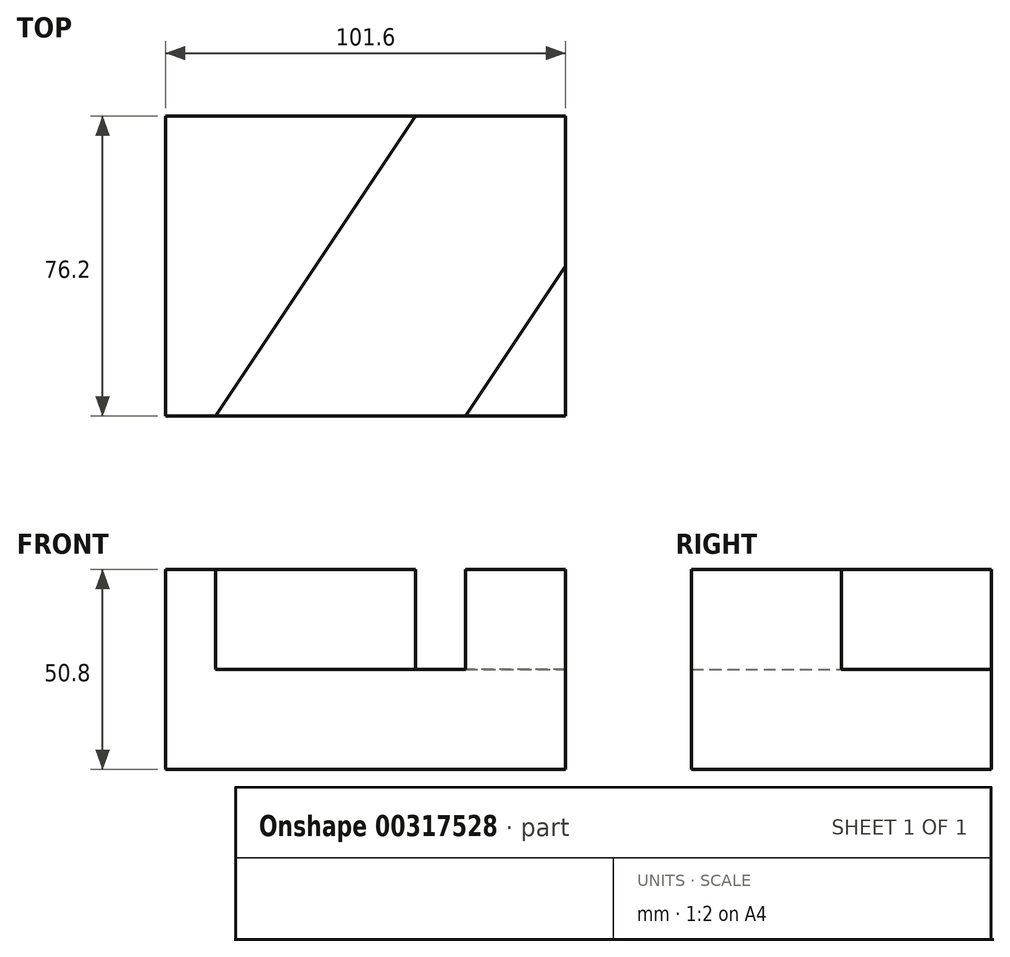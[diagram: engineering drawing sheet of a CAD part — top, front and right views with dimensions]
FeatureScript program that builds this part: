
annotation { "Feature Type Name" : "Feature", "Feature Type Description" : "" }
export const myFeature = defineFeature(function(context is Context, id is Id, definition is map)
    precondition{}
    {
        {
            var Q0;
            Q0=qCreatedBy(makeId("Top.planeOp"),FACE);
            var sketch = newSketch(context, id + "F0", { "sketchPlane" : qUnion([Q0])});
            skLineSegment(sketch, "E0", {"start": v(-51.3, -71.77) * mm, "end": v(50.3, -71.77) * mm});
            skLineSegment(sketch, "E1", {"start": v(50.3, -71.77) * mm, "end": v(50.3, 4.43) * mm});
            skLineSegment(sketch, "E2", {"start": v(50.3, 4.43) * mm, "end": v(-51.3, 4.43) * mm});
            skLineSegment(sketch, "E3", {"start": v(-51.3, 4.43) * mm, "end": v(-51.3, -71.77) * mm});
            skSolve(sketch);
        }
        {
            var Q0;
            Q0 = qSketchRegion(id + "F0", true);
            extrude(context, id + "F1", {"entities" : qUnion([Q0]), "depth" : 25.4 * mm});
        }
        {
            var Q0;
            Q0=makeQuery(id+"F1.opExtrude","CAP_FACE",FACE,{"disambiguationData":[OSD([sQuery(id+"F0.wireOp",EDGE,"E0"),sQuery(id+"F0.wireOp",EDGE,"E1"),sQuery(id+"F0.wireOp",EDGE,"E2"),sQuery(id+"F0.wireOp",EDGE,"E3")])],"isStart":false});
            var sketch = newSketch(context, id + "F2", { "sketchPlane" : qUnion([Q0])});
            skLineSegment(sketch, "E4", {"start": v(24.9, -71.77) * mm, "end": v(50.3, -71.77) * mm});
            skLineSegment(sketch, "E5", {"start": v(50.3, -71.77) * mm, "end": v(50.3, -33.67) * mm});
            skLineSegment(sketch, "E6", {"start": v(24.9, -71.77) * mm, "end": v(50.3, -33.67) * mm});
            skLineSegment(sketch, "E7", {"start": v(-51.3, -71.77) * mm, "end": v(-38.6, -71.77) * mm});
            skLineSegment(sketch, "E8", {"start": v(-51.3, -71.77) * mm, "end": v(-51.3, 4.43) * mm});
            skLineSegment(sketch, "E9", {"start": v(-51.3, 4.43) * mm, "end": v(12.2, 4.43) * mm});
            skLineSegment(sketch, "E10", {"start": v(-38.6, -71.77) * mm, "end": v(12.2, 4.43) * mm});
            skSolve(sketch);
        }
        {
            var Q0;
            Q0 = qSketchRegion(id + "F2", true);
            extrude(context, id + "F3", {"entities" : qUnion([Q0]), "operationType" : NewBodyOperationType.ADD, "depth" : 25.4 * mm});
        }
    });
